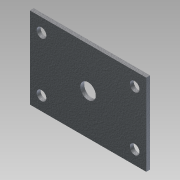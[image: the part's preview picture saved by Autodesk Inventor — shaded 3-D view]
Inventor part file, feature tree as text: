
AUTODESK INVENTOR PART (.ipt)
format: ipt  version: 2013 (Build 170138000, 138)  size: 115,200 bytes
history: native  units: in
note: dims shown in document units (in); Inventor stores cm internally (conversion verified against a paired STEP export)
features: extrude x3, sketch x3
ambient origin geometry x8: Origin, YZ Plane, XZ Plane, XY Plane, X Axis, Y Axis, Z Axis, Center Point
bodies: Solid1 (feature_tree)
feature tree (6):
  extrude  "Extrusion1"  Depth=3.75in
  extrude  "Extrusion2"  Depth=0.875in
  extrude  "Extrusion3"  Depth=0.875in
  sketch  "Sketch1"  dims[d0=2.625in d1=3.75in]
  sketch  "Sketch2"  dims[d2=0.125in d3=0.0in d4=0.875in]
  sketch  "Sketch3"  dims[d5=1.5in d6=0.875in d7=1.5in d8=0.3125in d9=0.3125in d10=0.3125in d11=0.3125in d12=0.125in d13=0.0in d14=0.5in d15=0.125in d16=0.0in]
